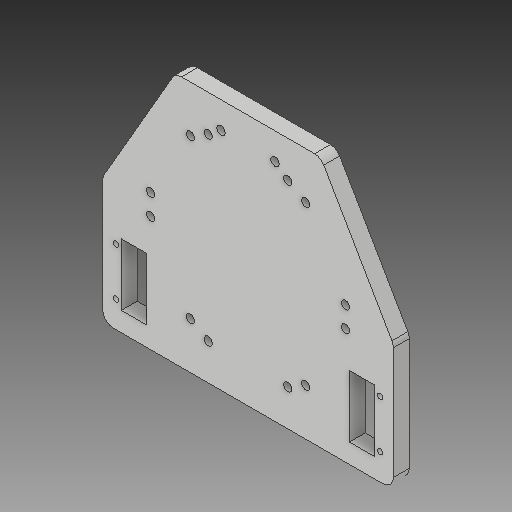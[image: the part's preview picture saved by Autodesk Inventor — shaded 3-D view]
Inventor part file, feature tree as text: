
AUTODESK INVENTOR PART (.ipt)
format: ipt  version: 2018 (Build 220112000, 112)  size: 201,728 bytes
history: native  units: mm
features: extrude x3, sketch x3, projected_geometry x2, fillet x1
ambient origin geometry x8: Origin, YZ Plane, XZ Plane, XY Plane, X Axis, Y Axis, Z Axis, Center Point
bodies: Solid1 (feature_tree)
feature tree (9):
  extrude  "Extrusion1"  TaperAngle=120.0deg  [1 undecoded]
  extrude  "Extrusion2"  Depth=47.462522mm
  extrude  "Extrusion3"  Depth=6.0mm TaperAngle=0.0deg
  fillet  "Fillet1"  Radius=2.02mm
  sketch  "Sketch1"  dims[d2=54.805mm d3=120.0deg]
  sketch  "Sketch2"  dims[d4=120.0deg d5=47.462522mm]
  projected_geometry  "Projected Loop1"
  sketch  "Sketch3"  dims[d6=47.462522mm d8=6.0mm d9=0.0mm d10=2.02mm d11=3.2mm d12=5.0mm d13=5.0mm d14=18.0mm d15=10.0mm d16=23.39mm d17=9.57mm d19=2.0mm d20=2.0mm d21=20.385mm d22=10.0mm d23=3.861382mm d24=6.0mm d25=0.0mm d26=3.1mm d27=39.0mm d28=4.5mm d29=4.5mm d30=4.5mm d31=4.5mm d32=4.5mm d33=4.5mm d34=4.5mm d35=4.5mm d36=4.5mm d37=4.5mm d38=10.0mm d39=0.0mm d40=59.755753mm d41=4.0mm]
  projected_geometry  "Projected Loop2"
note: 1 required parameter value undecoded (feature->parameter linkage not recoverable at this tier; creation-order binding heuristic only, values carry confidence <= 0.55)
